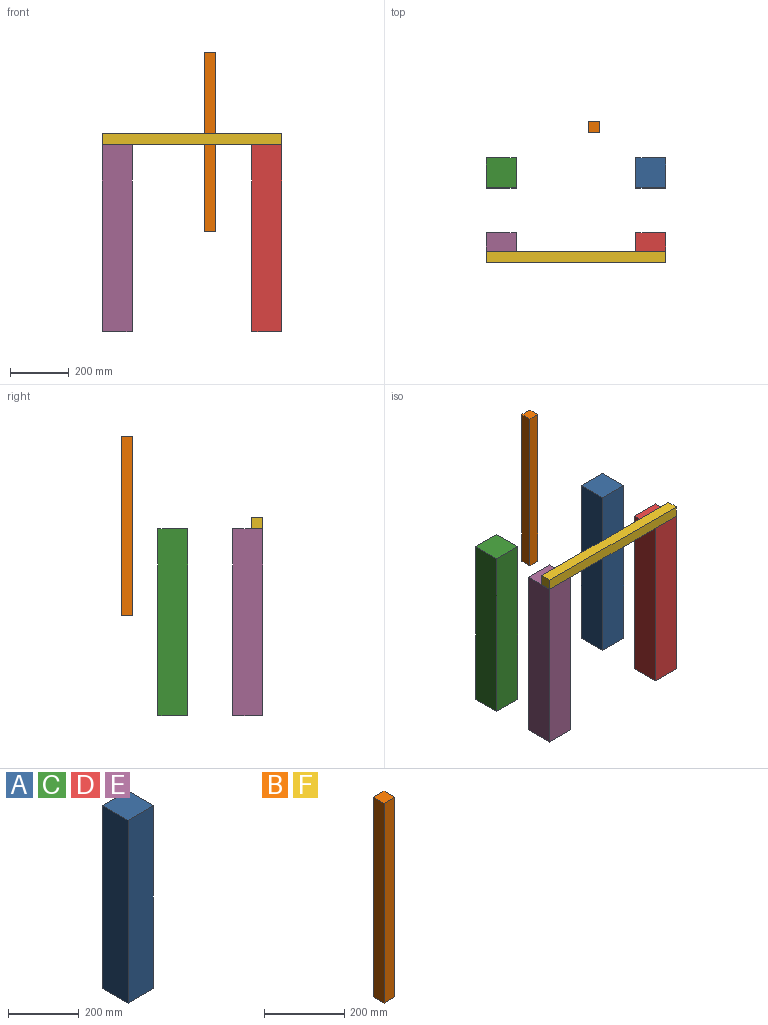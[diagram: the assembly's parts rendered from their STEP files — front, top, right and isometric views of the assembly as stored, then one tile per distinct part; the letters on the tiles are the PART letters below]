
ASSEMBLY  parts=6 mates=4
PART A: 6 faces, bbox 101.6x101.6x635 mm
  f0: plane 635x101.6mm, normal (-1,0,0), area 64516mm2, adj f1,f3,f4,f5
  f1: plane 101.6x101.6mm, normal (0,0,-1), area 10322.6mm2, adj f0,f2,f4,f5
  f2: plane 635x101.6mm, normal (1,0,0), area 64516mm2, adj f1,f3,f4,f5
  f3: plane 101.6x101.6mm, normal (0,0,1), area 10322.6mm2, adj f0,f2,f4,f5
  f4: plane 635x101.6mm, normal (0,1,0), area 64516mm2, adj f0,f1,f2,f3
  f5: plane 635x101.6mm, normal (0,-1,0), area 64516mm2, adj f0,f1,f2,f3
PART B: 6 faces, bbox 38.1x38.1x609.6 mm
  f0: plane 38.1x38.1mm, normal (0,0,-1), area 1451.6mm2, adj f1,f3,f4,f5
  f1: plane 609.6x38.1mm, normal (1,0,0), area 23225.8mm2, adj f0,f2,f4,f5
  f2: plane 38.1x38.1mm, normal (0,0,1), area 1451.6mm2, adj f1,f3,f4,f5
  f3: plane 609.6x38.1mm, normal (-1,0,0), area 23225.8mm2, adj f0,f2,f4,f5
  f4: plane 609.6x38.1mm, normal (0,-1,0), area 23225.8mm2, adj f0,f1,f2,f3
  f5: plane 609.6x38.1mm, normal (0,1,0), area 23225.8mm2, adj f0,f1,f2,f3
PART C: same geometry as A
PART D: same geometry as A
PART E: same geometry as A
PART F: same geometry as B
PLACE A rot(axis=(0,1,0),0deg) t=(226.76,375.55,90.98)mm
PLACE B t=(1.42,499.31,430.86)mm
PLACE C t=(-281.24,375.55,90.98)mm
PLACE D t=(226.76,121.55,90.98)mm
PLACE E t=(-281.24,121.55,90.98)mm
PLACE F rot(axis=(0,1,0),90deg) t=(-382.84,58.05,725.98)mm
MATE fastened C.f3 <-> E.f3  axis (0,0,1) through (-332.04,324.75,725.98)mm
MATE fastened F.f1 <-> D.f3  axis (0,0,1) through (226.76,19.95,725.98)mm
MATE fastened A.f3 <-> C.f3  axis (0,0,1) through (175.96,324.75,725.98)mm
MATE fastened D.f3 <-> E.f3  axis (0,0,1) through (175.96,70.75,725.98)mm
